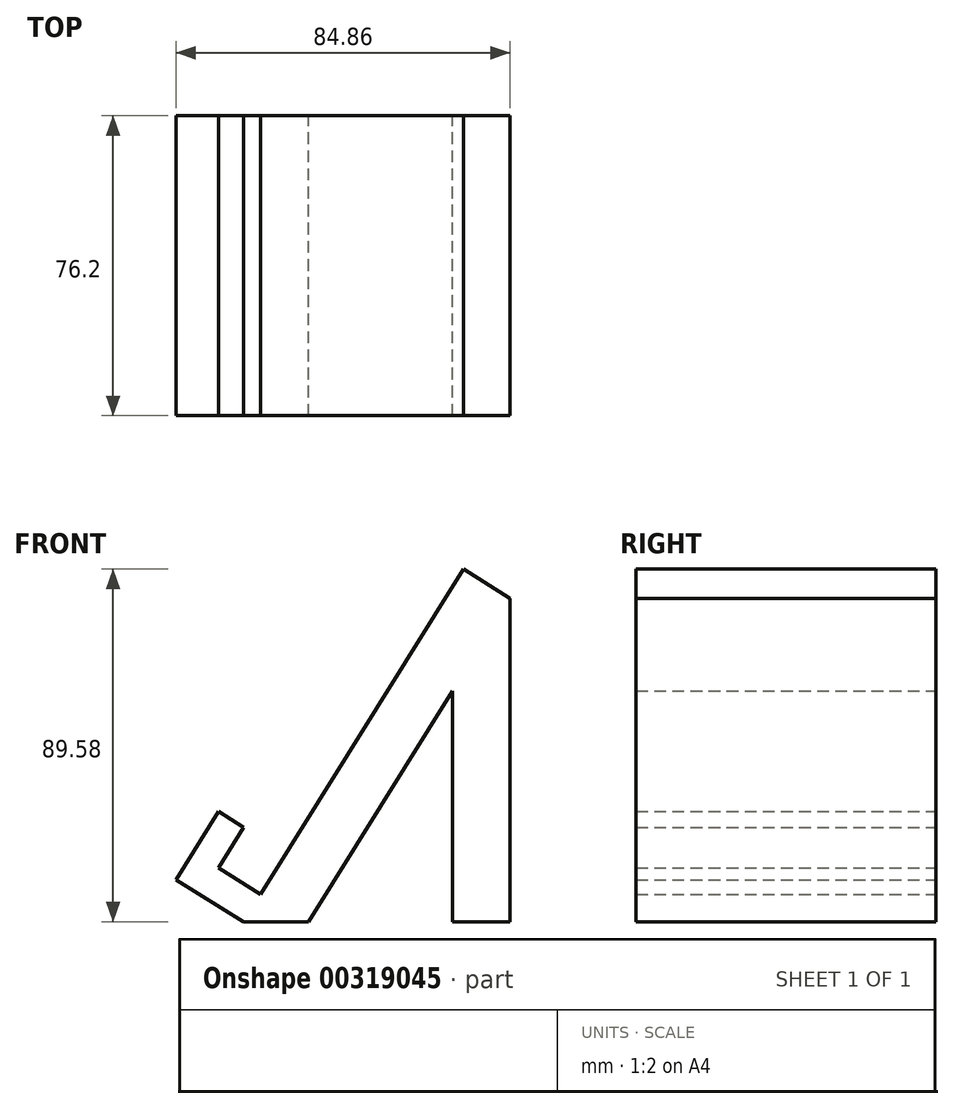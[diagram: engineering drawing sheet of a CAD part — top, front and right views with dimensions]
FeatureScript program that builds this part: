
annotation { "Feature Type Name" : "Feature", "Feature Type Description" : "" }
export const myFeature = defineFeature(function(context is Context, id is Id, definition is map)
    precondition{}
    {
        {
            var Q0;
            Q0=qCreatedBy(makeId("Front.planeOp"),FACE);
            var sketch = newSketch(context, id + "F0", { "sketchPlane" : qUnion([Q0])});
            skLineSegment(sketch, "E0", {"start": v(-27.37, 0) * mm, "end": v(28.43, 89.58) * mm});
            skLineSegment(sketch, "E1", {"start": v(28.43, 89.58) * mm, "end": v(40.33, 82.16) * mm});
            skLineSegment(sketch, "E2", {"start": v(40.33, 82.16) * mm, "end": v(-10.84, 0) * mm});
            skLineSegment(sketch, "E3", {"start": v(-10.84, 0) * mm, "end": v(-27.37, 0) * mm});
            skLineSegment(sketch, "E4", {"start": v(40.33, 82.16) * mm, "end": v(40.33, 0) * mm});
            skPoint(sketch, "E4.endSnap0", {"position": v(-19.1, 0) * mm});
            skLineSegment(sketch, "E5", {"start": v(40.33, 0) * mm, "end": v(25.7, 0) * mm});
            skLineSegment(sketch, "E6", {"start": v(25.7, 0) * mm, "end": v(25.7, 58.66) * mm});
            skLineSegment(sketch, "E7", {"start": v(-27.37, 0) * mm, "end": v(-10.84, 0) * mm});
            skLineSegment(sketch, "E8", {"start": v(-10.84, 0) * mm, "end": v(25.7, 0) * mm});
            skLineSegment(sketch, "E9", {"start": v(-27.37, 0) * mm, "end": v(-44.53, 10.7) * mm});
            skLineSegment(sketch, "E10", {"start": v(-44.53, 10.7) * mm, "end": v(-33.75, 28) * mm});
            skLineSegment(sketch, "E11", {"start": v(-33.75, 28) * mm, "end": v(-27.37, 24.02) * mm});
            skLineSegment(sketch, "E12", {"start": v(-27.37, 24.02) * mm, "end": v(-33.8, 13.68) * mm});
            skLineSegment(sketch, "E13", {"start": v(-33.8, 13.68) * mm, "end": v(-23.03, 6.96) * mm});
            skSolve(sketch);
        }
        {
            var Q0;
            {var subQ0=sQuery(id+"F0.wireOp",EDGE,"E9");Q0=makeQuery(id+"F0.imprint","IMPRINT",FACE,{"disambiguationData":[TD([[makeQuery(id+"F0.imprint","IMPRINT",EDGE,{"derivedFrom":subQ0}),-1.0]])]});}
            var Q1;
            {var subQ0=sQuery(id+"F0.wireOp",EDGE,"E4");Q1=makeQuery(id+"F0.imprint","IMPRINT",FACE,{"disambiguationData":[TD([[makeQuery(id+"F0.imprint","IMPRINT",EDGE,{"derivedFrom":subQ0}),-1.0]])]});}
            var Q2;
            {var subQ1=sQuery(id+"F0.wireOp",EDGE,"E1");Q2=makeQuery(id+"F0.imprint","IMPRINT",FACE,{"disambiguationData":[TD([[makeQuery(id+"F0.imprint","IMPRINT",EDGE,{"derivedFrom":subQ1}),-1.0]])]});}
            extrude(context, id + "F1", {"entities" : qUnion([Q0, Q1, Q2]), "depth" : 76.2 * mm});
        }
    });
